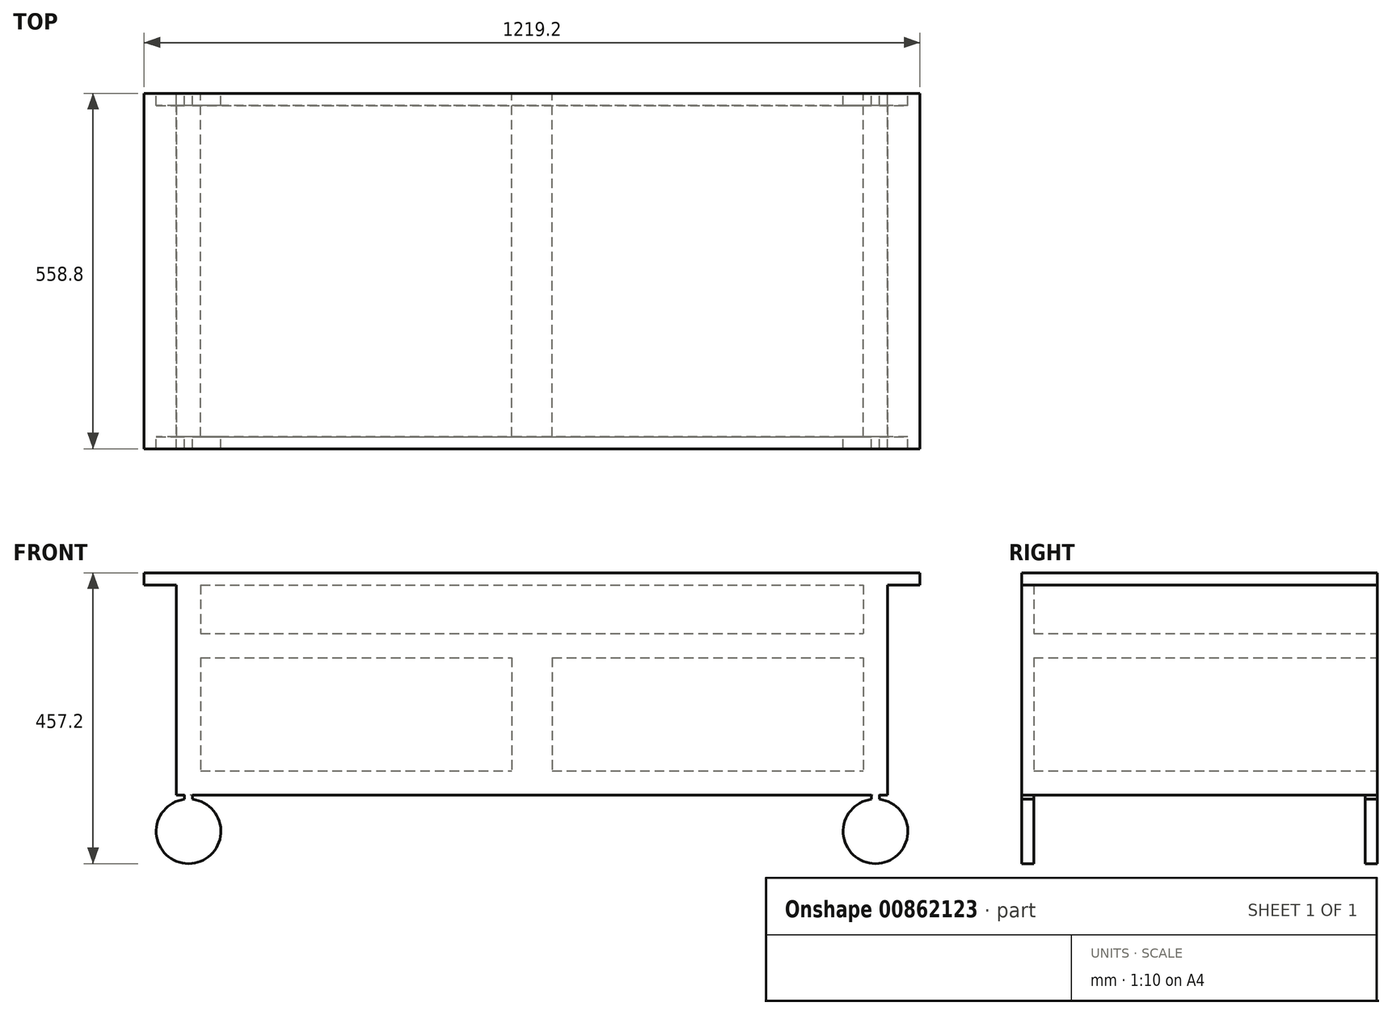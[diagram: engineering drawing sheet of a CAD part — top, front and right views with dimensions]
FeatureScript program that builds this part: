
annotation { "Feature Type Name" : "Feature", "Feature Type Description" : "" }
export const myFeature = defineFeature(function(context is Context, id is Id, definition is map)
    precondition{}
    {
        {
            var Q0;
            Q0=qCreatedBy(makeId("Front.planeOp"),FACE);
            var sketch = newSketch(context, id + "F0", { "sketchPlane" : qUnion([Q0])});
            skLineSegment(sketch, "E0.bottom", {"start": v(558.8, -165.1) * mm, "end": v(-558.8, -165.1) * mm});
            skLineSegment(sketch, "E0.top", {"start": v(558.8, 165.1) * mm, "end": v(-558.8, 165.1) * mm});
            skLineSegment(sketch, "E0.left", {"start": v(558.8, -165.1) * mm, "end": v(558.8, 165.1) * mm});
            skLineSegment(sketch, "E0.right", {"start": v(-558.8, -165.1) * mm, "end": v(-558.8, 165.1) * mm});
            skPoint(sketch, "E0.middle", {"position": v(0, 0) * mm});
            skLineSegment(sketch, "E1.bottom", {"start": v(-558.8, 165.1) * mm, "end": v(-520.7, 165.1) * mm});
            skLineSegment(sketch, "E1.top", {"start": v(-558.8, -165.1) * mm, "end": v(-520.7, -165.1) * mm});
            skLineSegment(sketch, "E1.left", {"start": v(-558.8, 165.1) * mm, "end": v(-558.8, -165.1) * mm});
            skLineSegment(sketch, "E1.right", {"start": v(-520.7, 165.1) * mm, "end": v(-520.7, -165.1) * mm});
            skLineSegment(sketch, "E2.bottom", {"start": v(558.8, 165.1) * mm, "end": v(520.7, 165.1) * mm});
            skLineSegment(sketch, "E2.top", {"start": v(558.8, -165.1) * mm, "end": v(520.7, -165.1) * mm});
            skLineSegment(sketch, "E2.left", {"start": v(558.8, 165.1) * mm, "end": v(558.8, -165.1) * mm});
            skLineSegment(sketch, "E2.right", {"start": v(520.7, 165.1) * mm, "end": v(520.7, -165.1) * mm});
            skLineSegment(sketch, "E3.bottom", {"start": v(-520.7, -165.1) * mm, "end": v(520.7, -165.1) * mm});
            skLineSegment(sketch, "E3.top", {"start": v(-520.7, -127) * mm, "end": v(520.7, -127) * mm});
            skLineSegment(sketch, "E3.left", {"start": v(-520.7, -165.1) * mm, "end": v(-520.7, -127) * mm});
            skLineSegment(sketch, "E3.right", {"start": v(520.7, -165.1) * mm, "end": v(520.7, -127) * mm});
            skLineSegment(sketch, "E4.bottom", {"start": v(-520.7, 165.1) * mm, "end": v(520.7, 165.1) * mm});
            skLineSegment(sketch, "E4.top", {"start": v(-520.7, 88.9) * mm, "end": v(520.7, 88.9) * mm});
            skLineSegment(sketch, "E4.left", {"start": v(-520.7, 165.1) * mm, "end": v(-520.7, 88.9) * mm});
            skLineSegment(sketch, "E4.right", {"start": v(520.7, 165.1) * mm, "end": v(520.7, 88.9) * mm});
            skLineSegment(sketch, "E5.top", {"start": v(-520.7, 50.8) * mm, "end": v(520.7, 50.8) * mm});
            skLineSegment(sketch, "E5.left", {"start": v(-520.7, 88.9) * mm, "end": v(-520.7, 50.8) * mm});
            skLineSegment(sketch, "E5.right", {"start": v(520.7, 88.9) * mm, "end": v(520.7, 50.8) * mm});
            skLineSegment(sketch, "E6.bottom", {"start": v(-609.6, 165.1) * mm, "end": v(609.6, 165.1) * mm});
            skLineSegment(sketch, "E6.top", {"start": v(-609.6, 184.15) * mm, "end": v(609.6, 184.15) * mm});
            skLineSegment(sketch, "E6.left", {"start": v(-609.6, 165.1) * mm, "end": v(-609.6, 184.15) * mm});
            skLineSegment(sketch, "E6.right", {"start": v(609.6, 165.1) * mm, "end": v(609.6, 184.15) * mm});
            skPoint(sketch, "E7.endSnap0", {"position": v(0, 184.15) * mm});
            skLineSegment(sketch, "E8", {"start": v(0, 89.47) * mm, "end": v(0, 371.76) * mm, "construction": true});
            skLineSegment(sketch, "E9.bottom", {"start": v(-31.75, 50.8) * mm, "end": v(31.75, 50.8) * mm});
            skLineSegment(sketch, "E9.top", {"start": v(-31.75, -127) * mm, "end": v(31.75, -127) * mm});
            skLineSegment(sketch, "E9.left", {"start": v(-31.75, 50.8) * mm, "end": v(-31.75, -127) * mm});
            skLineSegment(sketch, "E9.right", {"start": v(31.75, 50.8) * mm, "end": v(31.75, -127) * mm});
            skLineSegment(sketch, "E10", {"start": v(-539.75, -165.1) * mm, "end": v(-539.75, -222.25) * mm});
            skLineSegment(sketch, "E11", {"start": v(539.75, -165.1) * mm, "end": v(539.75, -222.25) * mm});
            skCircle(sketch, "E12", {"center": v(-539.75, -222.25) * mm, "radius": 50.8 * mm});
            skCircle(sketch, "E13", {"center": v(539.75, -222.25) * mm, "radius": 50.8 * mm});
            skLineSegment(sketch, "E14.bottom", {"start": v(-533.4, -182.13) * mm, "end": v(-546.1, -182.13) * mm});
            skLineSegment(sketch, "E14.top", {"start": v(-533.4, -148.07) * mm, "end": v(-546.1, -148.07) * mm});
            skLineSegment(sketch, "E14.left", {"start": v(-533.4, -182.13) * mm, "end": v(-533.4, -148.07) * mm});
            skLineSegment(sketch, "E14.right", {"start": v(-546.1, -182.13) * mm, "end": v(-546.1, -148.07) * mm});
            skPoint(sketch, "E14.middle", {"position": v(-539.75, -165.1) * mm});
            skLineSegment(sketch, "E15.bottom", {"start": v(546.1, -182.13) * mm, "end": v(533.4, -182.13) * mm});
            skLineSegment(sketch, "E15.top", {"start": v(546.1, -148.07) * mm, "end": v(533.4, -148.07) * mm});
            skLineSegment(sketch, "E15.left", {"start": v(546.1, -182.13) * mm, "end": v(546.1, -148.07) * mm});
            skLineSegment(sketch, "E15.right", {"start": v(533.4, -182.13) * mm, "end": v(533.4, -148.07) * mm});
            skPoint(sketch, "E15.middle", {"position": v(539.75, -165.1) * mm});
            skSolve(sketch);
        }
        {
            var Q0;
            {var subQ1=sQuery(id+"F0.wireOp",EDGE,"E14.top");Q0=makeQuery(id+"F0.imprint","IMPRINT",FACE,{"disambiguationData":[TD([[makeQuery(id+"F0.imprint","IMPRINT",EDGE,{"derivedFrom":subQ1}),1.0]])]});}
            var Q1;
            {var subQ4=sQuery(id+"F0.wireOp",EDGE,"E4.top");Q1=makeQuery(id+"F0.imprint","IMPRINT",FACE,{"disambiguationData":[TD([[makeQuery(id+"F0.imprint","IMPRINT",EDGE,{"derivedFrom":subQ4}),-1.0]])]});}
            var Q2;
            Q2=makeQuery(id+"F0.imprint","IMPRINT",FACE,{"disambiguationData":[TD([[makeQuery(id+"F0.imprint","IMPRINT",EDGE,{"derivedFrom":sQuery(id+"F0.wireOp",EDGE,"E6.top")}),-1.0]])]});
            var Q3;
            {var subQ1=sQuery(id+"F0.wireOp",EDGE,"E15.top");Q3=makeQuery(id+"F0.imprint","IMPRINT",FACE,{"disambiguationData":[TD([[makeQuery(id+"F0.imprint","IMPRINT",EDGE,{"derivedFrom":subQ1}),1.0]])]});}
            var Q4;
            {var subQ2=sQuery(id+"F0.wireOp",EDGE,"E2.right");var subQ4=sQuery(id+"F0.wireOp",EDGE,"E0.bottom");var subQ5=makeQuery(id+"F0.imprint","INTERSECT",VERTEX,{"derivedFrom":[subQ4,subQ2]});Q4=makeQuery(id+"F0.imprint","IMPRINT",FACE,{"disambiguationData":[TD([[makeQuery(id+"F0.imprint","IMPRINT",EDGE,{"disambiguationData":[TD([[subQ5,-1.0]])],"derivedFrom":subQ4}),-1.0]])]});}
            var Q5;
            {var subQ2=sQuery(id+"F0.wireOp",EDGE,"E9.left");Q5=makeQuery(id+"F0.imprint","IMPRINT",FACE,{"disambiguationData":[TD([[makeQuery(id+"F0.imprint","IMPRINT",EDGE,{"derivedFrom":subQ2}),1.0]])]});}
            var Q6;
            {var subQ4=sQuery(id+"F0.wireOp",EDGE,"E0.left");Q6=makeQuery(id+"F0.imprint","IMPRINT",FACE,{"disambiguationData":[TD([[makeQuery(id+"F0.imprint","IMPRINT",EDGE,{"derivedFrom":subQ4}),1.0]])]});}
            var Q7;
            {var subQ11=sQuery(id+"F0.wireOp",EDGE,"E0.right");Q7=makeQuery(id+"F0.imprint","IMPRINT",FACE,{"disambiguationData":[TD([[makeQuery(id+"F0.imprint","IMPRINT",EDGE,{"derivedFrom":subQ11}),-1.0]])]});}
            var Q8;
            {var subQ0=sQuery(id+"F0.wireOp",EDGE,"E10");var subQ1=sQuery(id+"F0.wireOp",EDGE,"E0.bottom");var subQ2=makeQuery(id+"F0.imprint","INTERSECT",VERTEX,{"derivedFrom":[subQ1,subQ0]});Q8=makeQuery(id+"F0.imprint","IMPRINT",FACE,{"disambiguationData":[TD([[makeQuery(id+"F0.imprint","IMPRINT",EDGE,{"disambiguationData":[TD([[subQ2,-1.0]])],"derivedFrom":subQ1}),1.0]])]});}
            var Q9;
            {var subQ0=sQuery(id+"F0.wireOp",EDGE,"E10");var subQ1=sQuery(id+"F0.wireOp",EDGE,"E0.bottom");var subQ2=makeQuery(id+"F0.imprint","INTERSECT",VERTEX,{"derivedFrom":[subQ1,subQ0]});Q9=makeQuery(id+"F0.imprint","IMPRINT",FACE,{"disambiguationData":[TD([[makeQuery(id+"F0.imprint","IMPRINT",EDGE,{"disambiguationData":[TD([[subQ2,1.0]])],"derivedFrom":subQ1}),1.0]])]});}
            var Q10;
            {var subQ0=sQuery(id+"F0.wireOp",EDGE,"E14.bottom");var subQ1=sQuery(id+"F0.wireOp",EDGE,"E10");var subQ2=makeQuery(id+"F0.imprint","INTERSECT",VERTEX,{"derivedFrom":[subQ1,subQ0]});Q10=makeQuery(id+"F0.imprint","IMPRINT",FACE,{"disambiguationData":[TD([[makeQuery(id+"F0.imprint","IMPRINT",EDGE,{"disambiguationData":[TD([[subQ2,1.0]])],"derivedFrom":subQ1}),1.0]])]});}
            var Q11;
            {var subQ0=sQuery(id+"F0.wireOp",EDGE,"E14.bottom");var subQ1=sQuery(id+"F0.wireOp",EDGE,"E10");var subQ2=makeQuery(id+"F0.imprint","INTERSECT",VERTEX,{"derivedFrom":[subQ1,subQ0]});Q11=makeQuery(id+"F0.imprint","IMPRINT",FACE,{"disambiguationData":[TD([[makeQuery(id+"F0.imprint","IMPRINT",EDGE,{"disambiguationData":[TD([[subQ2,1.0]])],"derivedFrom":subQ1}),-1.0]])]});}
            var Q12;
            {var subQ0=sQuery(id+"F0.wireOp",EDGE,"E14.left");var subQ3=sQuery(id+"F0.wireOp",EDGE,"E12");var subQ4=makeQuery(id+"F0.imprint","INTERSECT",VERTEX,{"derivedFrom":[subQ3,subQ0]});Q12=makeQuery(id+"F0.imprint","IMPRINT",FACE,{"disambiguationData":[TD([[makeQuery(id+"F0.imprint","IMPRINT",EDGE,{"disambiguationData":[TD([[subQ4,1.0]])],"derivedFrom":subQ3}),1.0]])]});}
            var Q13;
            {var subQ0=sQuery(id+"F0.wireOp",EDGE,"E15.right");var subQ1=sQuery(id+"F0.wireOp",EDGE,"E0.bottom");var subQ2=makeQuery(id+"F0.imprint","INTERSECT",VERTEX,{"derivedFrom":[subQ1,subQ0]});Q13=makeQuery(id+"F0.imprint","IMPRINT",FACE,{"disambiguationData":[TD([[makeQuery(id+"F0.imprint","IMPRINT",EDGE,{"disambiguationData":[TD([[subQ2,1.0]])],"derivedFrom":subQ1}),1.0]])]});}
            var Q14;
            {var subQ0=sQuery(id+"F0.wireOp",EDGE,"E15.bottom");var subQ1=sQuery(id+"F0.wireOp",EDGE,"E11");var subQ2=makeQuery(id+"F0.imprint","INTERSECT",VERTEX,{"derivedFrom":[subQ1,subQ0]});Q14=makeQuery(id+"F0.imprint","IMPRINT",FACE,{"disambiguationData":[TD([[makeQuery(id+"F0.imprint","IMPRINT",EDGE,{"disambiguationData":[TD([[subQ2,1.0]])],"derivedFrom":subQ1}),-1.0]])]});}
            var Q15;
            {var subQ0=sQuery(id+"F0.wireOp",EDGE,"E15.left");var subQ1=sQuery(id+"F0.wireOp",EDGE,"E0.bottom");var subQ2=makeQuery(id+"F0.imprint","INTERSECT",VERTEX,{"derivedFrom":[subQ1,subQ0]});Q15=makeQuery(id+"F0.imprint","IMPRINT",FACE,{"disambiguationData":[TD([[makeQuery(id+"F0.imprint","IMPRINT",EDGE,{"disambiguationData":[TD([[subQ2,-1.0]])],"derivedFrom":subQ1}),1.0]])]});}
            var Q16;
            {var subQ0=sQuery(id+"F0.wireOp",EDGE,"E15.bottom");var subQ1=sQuery(id+"F0.wireOp",EDGE,"E11");var subQ2=makeQuery(id+"F0.imprint","INTERSECT",VERTEX,{"derivedFrom":[subQ1,subQ0]});Q16=makeQuery(id+"F0.imprint","IMPRINT",FACE,{"disambiguationData":[TD([[makeQuery(id+"F0.imprint","IMPRINT",EDGE,{"disambiguationData":[TD([[subQ2,1.0]])],"derivedFrom":subQ1}),1.0]])]});}
            var Q17;
            {var subQ0=sQuery(id+"F0.wireOp",EDGE,"E15.left");var subQ3=sQuery(id+"F0.wireOp",EDGE,"E13");var subQ4=makeQuery(id+"F0.imprint","INTERSECT",VERTEX,{"derivedFrom":[subQ3,subQ0]});Q17=makeQuery(id+"F0.imprint","IMPRINT",FACE,{"disambiguationData":[TD([[makeQuery(id+"F0.imprint","IMPRINT",EDGE,{"disambiguationData":[TD([[subQ4,1.0]])],"derivedFrom":subQ3}),1.0]])]});}
            extrude(context, id + "F1", {"entities" : qUnion([Q0, Q1, Q2, Q3, Q4, Q5, Q6, Q7, Q8, Q9, Q10, Q11, Q12, Q13, Q14, Q15, Q16, Q17]), "depth" : 558.8 * mm, "offsetDistance" : 25.4 * mm});
        }
        {
            var Q0;
            Q0=makeQuery(id+"F1.opExtrude","SWEPT_FACE",FACE,{"disambiguationData":[OSD([sQuery(id+"F0.wireOp",EDGE,"E0.right")])]});
            cPlane(context, id + "F2", {"entities" : qUnion([Q0]), "cplaneType" : CPlaneType.OFFSET, "offset" : 203.2 * mm, "width" : 152.4 * mm, "height" : 152.4 * mm});
        }
        {
            var Q0;
            Q0=qCreatedBy(id+"F2.planeOp",FACE);
            var sketch = newSketch(context, id + "F3", { "sketchPlane" : qUnion([Q0])});
            skLineSegment(sketch, "E16.bottom", {"start": v(0, -165.07) * mm, "end": v(19.05, -165.07) * mm});
            skLineSegment(sketch, "E16.top", {"start": v(0, -171.57) * mm, "end": v(19.05, -171.57) * mm});
            skLineSegment(sketch, "E16.left", {"start": v(0, -165.07) * mm, "end": v(0, -171.57) * mm});
            skLineSegment(sketch, "E16.right", {"start": v(19.05, -165.07) * mm, "end": v(19.05, -171.57) * mm});
            skLineSegment(sketch, "E17.bottom", {"start": v(559.12, -165.07) * mm, "end": v(540.07, -165.07) * mm});
            skLineSegment(sketch, "E17.top", {"start": v(559.12, -173.71) * mm, "end": v(540.07, -173.71) * mm});
            skLineSegment(sketch, "E17.left", {"start": v(559.12, -165.07) * mm, "end": v(559.12, -173.71) * mm});
            skLineSegment(sketch, "E17.right", {"start": v(540.07, -165.07) * mm, "end": v(540.07, -173.71) * mm});
            skLineSegment(sketch, "E18.bottom", {"start": v(19.05, -165.07) * mm, "end": v(540.07, -165.07) * mm});
            skLineSegment(sketch, "E18.top", {"start": v(19.05, -304.82) * mm, "end": v(540.07, -304.82) * mm});
            skLineSegment(sketch, "E18.left", {"start": v(19.05, -165.07) * mm, "end": v(19.05, -304.82) * mm});
            skLineSegment(sketch, "E18.right", {"start": v(540.07, -165.07) * mm, "end": v(540.07, -304.82) * mm});
            skSolve(sketch);
        }
        {
            var Q0;
            Q0=makeQuery(id+"F3.imprint","IMPRINT",FACE,{"disambiguationData":[TD([[makeQuery(id+"F3.imprint","IMPRINT",EDGE,{"derivedFrom":sQuery(id+"F3.wireOp",EDGE,"E16.right")}),1.0]])]});
            extrude(context, id + "F4", {"entities" : qUnion([Q0]), "operationType" : NewBodyOperationType.REMOVE, "oppositeDirection" : true, "depth" : 1412.24 * mm, "offsetDistance" : 25.4 * mm});
        }
        {
            var Q0;
            Q0=makeQuery(id+"F1.opExtrude","SWEPT_FACE",FACE,{"disambiguationData":[OSD([sQuery(id+"F0.wireOp",EDGE,"E0.left")])]});
            var sketch = newSketch(context, id + "F5", { "sketchPlane" : qUnion([Q0])});
            skLineSegment(sketch, "E19.bottom", {"start": v(-558.8, 165.1) * mm, "end": v(-540.07, 165.1) * mm});
            skLineSegment(sketch, "E19.top", {"start": v(-558.8, -165.07) * mm, "end": v(-540.07, -165.07) * mm});
            skLineSegment(sketch, "E19.left", {"start": v(-558.8, 165.1) * mm, "end": v(-558.8, -165.07) * mm});
            skLineSegment(sketch, "E19.right", {"start": v(-540.07, 165.1) * mm, "end": v(-540.07, -165.07) * mm});
            skSolve(sketch);
        }
        {
            var Q0;
            Q0=makeQuery(id+"F5.imprint","IMPRINT",FACE,{"disambiguationData":[TD([[makeQuery(id+"F5.imprint","IMPRINT",EDGE,{"derivedFrom":sQuery(id+"F5.wireOp",EDGE,"E19.bottom")}),-1.0]])]});
            extrude(context, id + "F6", {"entities" : qUnion([Q0]), "operationType" : NewBodyOperationType.ADD, "oppositeDirection" : true, "depth" : 1117.6 * mm, "offsetDistance" : 25.4 * mm});
        }
    });
